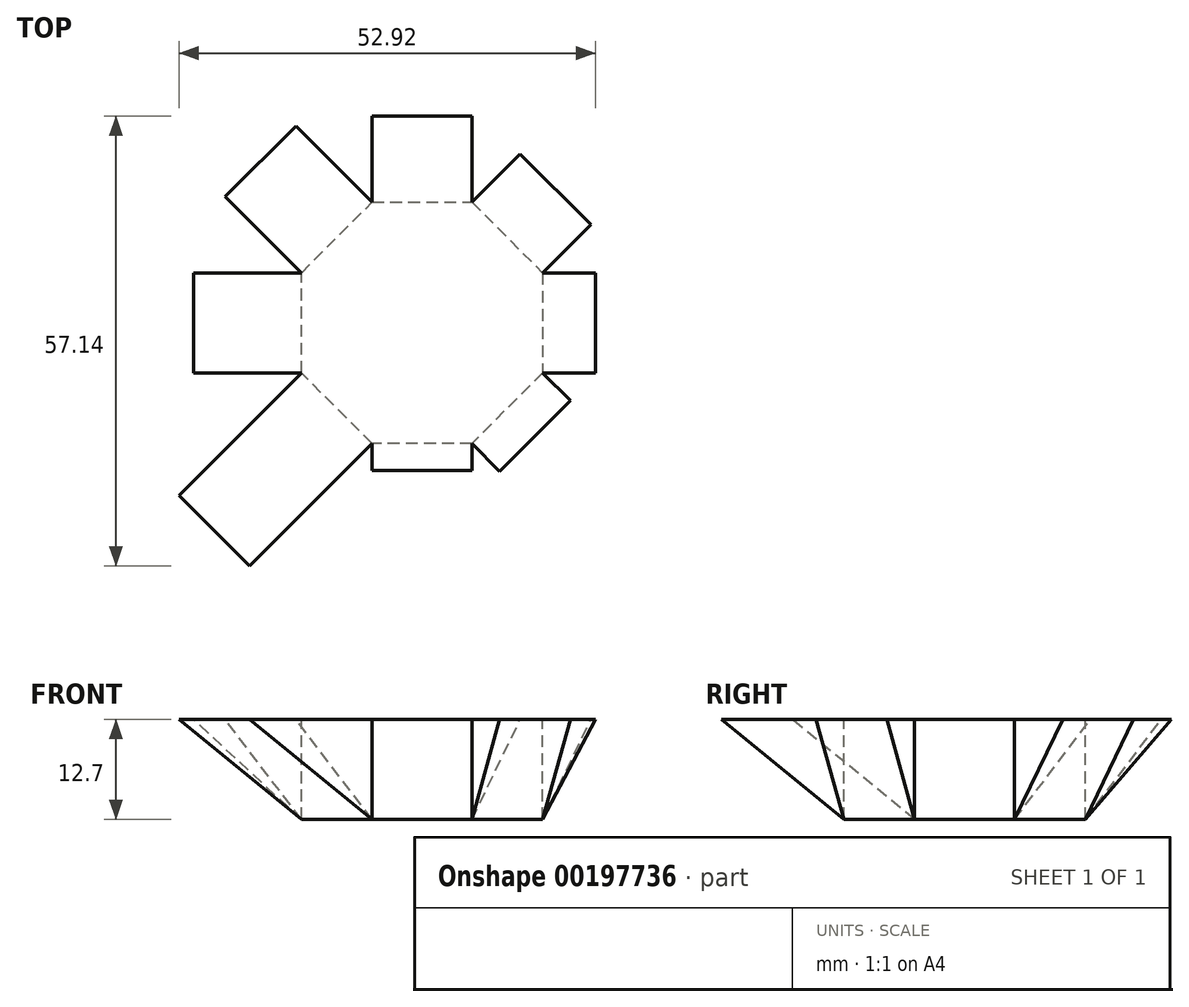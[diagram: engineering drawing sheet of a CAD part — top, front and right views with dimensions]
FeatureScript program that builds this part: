
annotation { "Feature Type Name" : "Feature", "Feature Type Description" : "" }
export const myFeature = defineFeature(function(context is Context, id is Id, definition is map)
    precondition{}
    {
        {
            var Q0;
            Q0=qCreatedBy(makeId("Top.planeOp"),FACE);
            var sketch = newSketch(context, id + "F0", { "sketchPlane" : qUnion([Q0])});
            skCircle(sketch, "E0.cCircle", {"center": v(0, 0) * mm, "radius": 16.6 * mm, "construction": true});
            skLineSegment(sketch, "E0.0", {"start": v(15.33, -6.35) * mm, "end": v(6.35, -15.33) * mm});
            skLineSegment(sketch, "E0.1", {"start": v(6.35, -15.33) * mm, "end": v(-6.35, -15.33) * mm});
            skLineSegment(sketch, "E0.2", {"start": v(-6.35, -15.33) * mm, "end": v(-15.33, -6.35) * mm});
            skLineSegment(sketch, "E0.3", {"start": v(-15.33, -6.35) * mm, "end": v(-15.33, 6.35) * mm});
            skLineSegment(sketch, "E0.4", {"start": v(-15.33, 6.35) * mm, "end": v(-6.35, 15.33) * mm});
            skLineSegment(sketch, "E0.5", {"start": v(-6.35, 15.33) * mm, "end": v(6.35, 15.33) * mm});
            skLineSegment(sketch, "E0.6", {"start": v(6.35, 15.33) * mm, "end": v(15.33, 6.35) * mm});
            skLineSegment(sketch, "E0.7", {"start": v(15.33, 6.35) * mm, "end": v(15.33, -6.35) * mm});
            skSolve(sketch);
        }
        {
            var Q0;
            Q0 = qSketchRegion(id + "F0", true);
            extrude(context, id + "F1", {"entities" : qUnion([Q0]), "oppositeDirection" : true, "depth" : 12.7 * mm});
        }
        {
            var Q0;
            Q0=makeQuery(id+"F1.opExtrude","SWEPT_FACE",FACE,{"disambiguationData":[OSD([sQuery(id+"F0.wireOp",EDGE,"E0.0")])]});
            var Q1;
            Q1=makeQuery(id+"F1.opExtrude","SWEPT_FACE",FACE,{"disambiguationData":[OSD([sQuery(id+"F0.wireOp",EDGE,"E0.4")])]});
            cPlane(context, id + "F2", {"entities" : qUnion([Q0, Q1]), "cplaneType" : CPlaneType.MID_PLANE, "offset" : 25.4 * mm, "width" : 152.4 * mm, "height" : 152.4 * mm});
        }
        {
            var Q0;
            Q0=makeQuery(id+"F1.opExtrude","SWEPT_FACE",FACE,{"disambiguationData":[OSD([sQuery(id+"F0.wireOp",EDGE,"E0.2")])]});
            var Q1;
            Q1=makeQuery(id+"F1.opExtrude","SWEPT_FACE",FACE,{"disambiguationData":[OSD([sQuery(id+"F0.wireOp",EDGE,"E0.6")])]});
            cPlane(context, id + "F3", {"entities" : qUnion([Q0, Q1]), "cplaneType" : CPlaneType.MID_PLANE, "offset" : 25.4 * mm, "width" : 152.4 * mm, "height" : 152.4 * mm});
        }
        {
            var Q0;
            Q0=qCreatedBy(makeId("Right.planeOp"),FACE);
            var sketch = newSketch(context, id + "F4", { "sketchPlane" : qUnion([Q0])});
            skLineSegment(sketch, "E1", {"start": v(-15.33, 0) * mm, "end": v(-15.33, -12.7) * mm});
            skLineSegment(sketch, "E2", {"start": v(-15.33, -12.7) * mm, "end": v(-18.73, 0) * mm});
            skLineSegment(sketch, "E3", {"start": v(-18.73, 0) * mm, "end": v(-15.33, 0) * mm});
            skSolve(sketch);
        }
        {
            var Q0;
            Q0=makeQuery(id+"F4.imprint","IMPRINT",FACE,{"disambiguationData":[TD([[makeQuery(id+"F4.imprint","IMPRINT",EDGE,{"derivedFrom":sQuery(id+"F4.wireOp",EDGE,"E1")}),-1.0]])]});
            extrude(context, id + "F5", {"entities" : qUnion([Q0]), "operationType" : NewBodyOperationType.ADD, "endBound" : BoundingType.SYMMETRIC, "oppositeDirection" : true, "depth" : 12.7 * mm, "hasSecondDirection" : true, "secondDirectionBound" : SecondDirectionBoundingType.UP_TO_SURFACE, "secondDirectionOppositeDirection" : false, "secondDirectionDepth" : 25.4 * mm});
        }
        {
            var Q0;
            Q0=qCreatedBy(id+"F3.planeOp",FACE);
            var sketch = newSketch(context, id + "F6", { "sketchPlane" : qUnion([Q0])});
            skLineSegment(sketch, "E4", {"start": v(15.33, 0) * mm, "end": v(15.33, -12.7) * mm});
            skLineSegment(sketch, "E5", {"start": v(15.33, -12.7) * mm, "end": v(20.31, 0) * mm});
            skLineSegment(sketch, "E6", {"start": v(20.31, 0) * mm, "end": v(15.33, 0) * mm});
            skSolve(sketch);
        }
        {
            var Q0;
            Q0 = qSketchRegion(id + "F6", true);
            extrude(context, id + "F7", {"entities" : qUnion([Q0]), "operationType" : NewBodyOperationType.ADD, "endBound" : BoundingType.SYMMETRIC, "depth" : 12.7 * mm});
        }
        {
            var Q0;
            Q0=qCreatedBy(makeId("Front.planeOp"),FACE);
            var sketch = newSketch(context, id + "F8", { "sketchPlane" : qUnion([Q0])});
            skLineSegment(sketch, "E7", {"start": v(15.33, 0) * mm, "end": v(15.33, -12.7) * mm});
            skLineSegment(sketch, "E8", {"start": v(15.33, -12.7) * mm, "end": v(22.04, 0) * mm});
            skLineSegment(sketch, "E9", {"start": v(22.04, 0) * mm, "end": v(15.33, 0) * mm});
            skSolve(sketch);
        }
        {
            var Q0;
            Q0 = qSketchRegion(id + "F8", true);
            extrude(context, id + "F9", {"entities" : qUnion([Q0]), "operationType" : NewBodyOperationType.ADD, "endBound" : BoundingType.SYMMETRIC, "depth" : 12.7 * mm});
        }
        {
            var Q0;
            Q0=qCreatedBy(id+"F2.planeOp",FACE);
            var sketch = newSketch(context, id + "F10", { "sketchPlane" : qUnion([Q0])});
            skLineSegment(sketch, "E10", {"start": v(15.33, 0) * mm, "end": v(15.33, -12.7) * mm});
            skLineSegment(sketch, "E11", {"start": v(15.33, -12.7) * mm, "end": v(23.99, 0) * mm});
            skLineSegment(sketch, "E12", {"start": v(23.99, 0) * mm, "end": v(15.33, 0) * mm});
            skSolve(sketch);
        }
        {
            var Q0;
            Q0 = qSketchRegion(id + "F10", true);
            extrude(context, id + "F11", {"entities" : qUnion([Q0]), "operationType" : NewBodyOperationType.ADD, "endBound" : BoundingType.SYMMETRIC, "depth" : 12.7 * mm});
        }
        {
            var Q0;
            Q0=qCreatedBy(makeId("Right.planeOp"),FACE);
            var sketch = newSketch(context, id + "F12", { "sketchPlane" : qUnion([Q0])});
            skLineSegment(sketch, "E13", {"start": v(15.33, 0) * mm, "end": v(15.33, -12.7) * mm});
            skLineSegment(sketch, "E14", {"start": v(15.33, -12.7) * mm, "end": v(26.26, 0) * mm});
            skLineSegment(sketch, "E15", {"start": v(26.26, 0) * mm, "end": v(15.33, 0) * mm});
            skSolve(sketch);
        }
        {
            var Q0;
            Q0 = qSketchRegion(id + "F12", true);
            extrude(context, id + "F13", {"entities" : qUnion([Q0]), "operationType" : NewBodyOperationType.ADD, "endBound" : BoundingType.SYMMETRIC, "depth" : 12.7 * mm});
        }
        {
            var Q0;
            Q0=qCreatedBy(id+"F3.planeOp",FACE);
            var sketch = newSketch(context, id + "F14", { "sketchPlane" : qUnion([Q0])});
            skLineSegment(sketch, "E16", {"start": v(-15.33, 0) * mm, "end": v(-15.33, -12.7) * mm});
            skLineSegment(sketch, "E17", {"start": v(-15.33, -12.7) * mm, "end": v(-29.02, 0) * mm});
            skLineSegment(sketch, "E18", {"start": v(-29.02, 0) * mm, "end": v(-15.33, 0) * mm});
            skSolve(sketch);
        }
        {
            var Q0;
            Q0=makeQuery(id+"F14.imprint","IMPRINT",FACE,{"disambiguationData":[TD([[makeQuery(id+"F14.imprint","IMPRINT",EDGE,{"derivedFrom":sQuery(id+"F14.wireOp",EDGE,"E16")}),-1.0]])]});
            extrude(context, id + "F15", {"entities" : qUnion([Q0]), "operationType" : NewBodyOperationType.ADD, "endBound" : BoundingType.SYMMETRIC, "depth" : 12.7 * mm});
        }
        {
            var Q0;
            Q0=qCreatedBy(makeId("Front.planeOp"),FACE);
            var sketch = newSketch(context, id + "F16", { "sketchPlane" : qUnion([Q0])});
            skLineSegment(sketch, "E19", {"start": v(-15.33, 0) * mm, "end": v(-15.33, -12.7) * mm});
            skLineSegment(sketch, "E20", {"start": v(-15.33, -12.7) * mm, "end": v(-29.02, 0) * mm});
            skLineSegment(sketch, "E21", {"start": v(-29.02, 0) * mm, "end": v(-15.33, 0) * mm});
            skSolve(sketch);
        }
        {
            var Q0;
            Q0 = qSketchRegion(id + "F16", true);
            extrude(context, id + "F17", {"entities" : qUnion([Q0]), "operationType" : NewBodyOperationType.ADD, "endBound" : BoundingType.SYMMETRIC, "depth" : 12.7 * mm});
        }
        {
            var Q0;
            Q0=qCreatedBy(id+"F2.planeOp",FACE);
            var sketch = newSketch(context, id + "F18", { "sketchPlane" : qUnion([Q0])});
            skLineSegment(sketch, "E22", {"start": v(-15.33, 0) * mm, "end": v(-15.33, -12.7) * mm});
            skLineSegment(sketch, "E23", {"start": v(-15.33, -12.7) * mm, "end": v(-37.33, 0) * mm});
            skLineSegment(sketch, "E24", {"start": v(-37.33, 0) * mm, "end": v(-15.33, 0) * mm});
            skSolve(sketch);
        }
        {
            var Q0;
            Q0 = qSketchRegion(id + "F18", true);
            extrude(context, id + "F19", {"entities" : qUnion([Q0]), "operationType" : NewBodyOperationType.ADD, "endBound" : BoundingType.SYMMETRIC, "depth" : 12.7 * mm});
        }
    });
